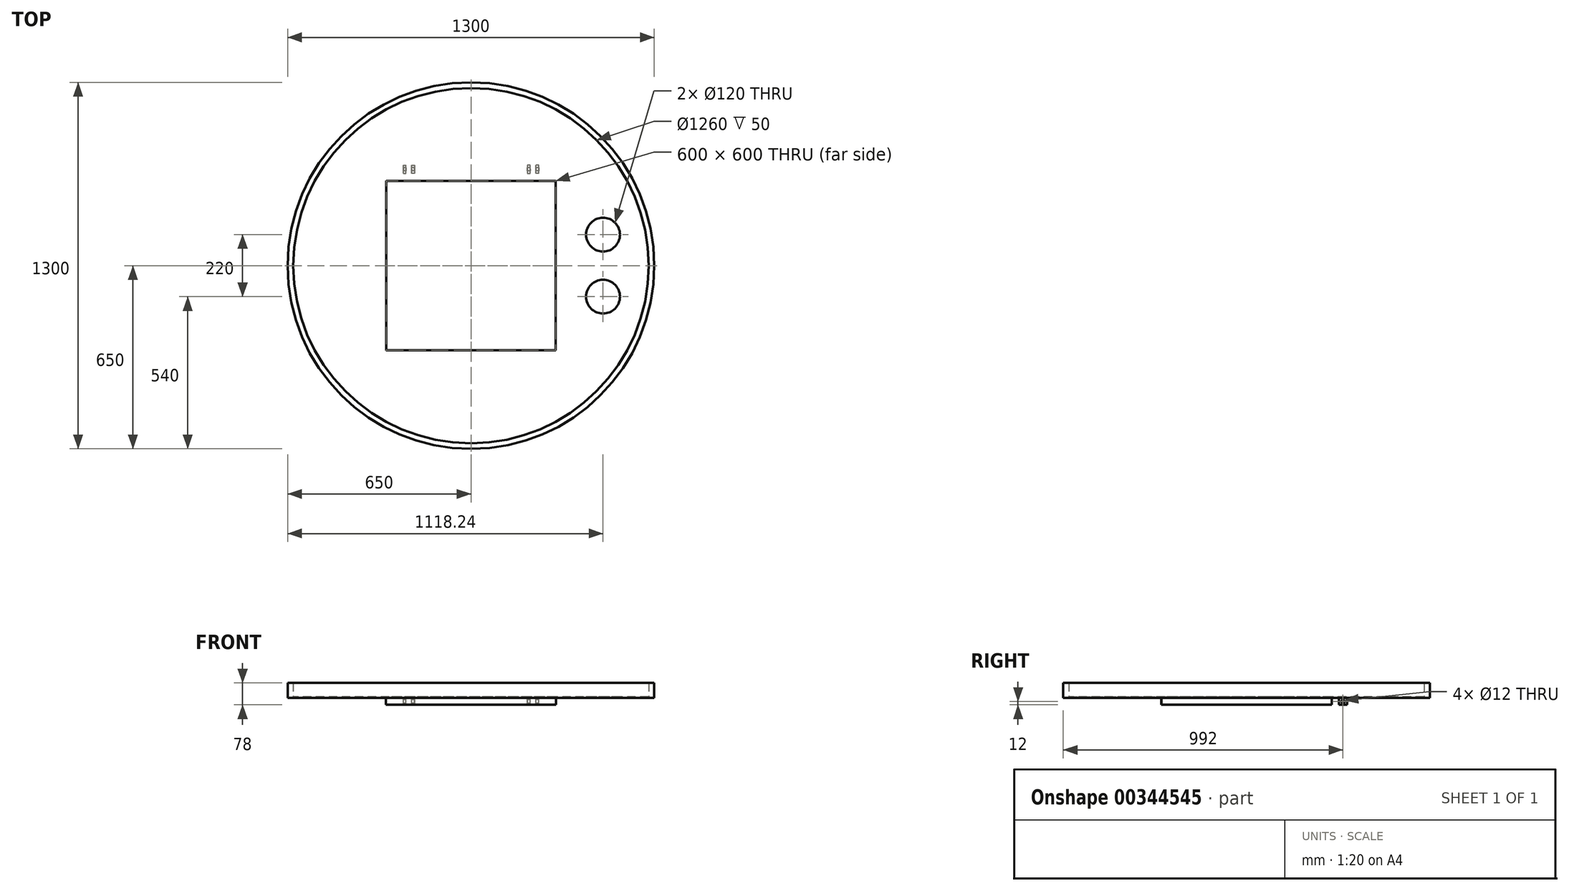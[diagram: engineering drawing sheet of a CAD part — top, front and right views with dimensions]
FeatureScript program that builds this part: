
annotation { "Feature Type Name" : "Feature", "Feature Type Description" : "" }
export const myFeature = defineFeature(function(context is Context, id is Id, definition is map)
    precondition{}
    {
        {
            var Q0;
            Q0=qCreatedBy(makeId("Top.planeOp"),FACE);
            var sketch = newSketch(context, id + "F0", { "sketchPlane" : qUnion([Q0])});
            skCircle(sketch, "E0", {"center": v(0, 0) * mm, "radius": 650 * mm});
            skSolve(sketch);
        }
        {
            var Q0;
            Q0=makeQuery(id+"F0.imprint","IMPRINT",FACE,{"disambiguationData":[TD([[makeQuery(id+"F0.imprint","IMPRINT",EDGE,{"derivedFrom":sQuery(id+"F0.wireOp",EDGE,"E0")}),1.0]])]});
            extrude(context, id + "F1", {"entities" : qUnion([Q0]), "depth" : 3 * mm});
        }
        {
            var Q0;
            Q0=makeQuery(id+"F1.opExtrude","CAP_FACE",FACE,{"disambiguationData":[OSD([sQuery(id+"F0.wireOp",EDGE,"E0")])],"isStart":false});
            var sketch = newSketch(context, id + "F2", { "sketchPlane" : qUnion([Q0])});
            skCircle(sketch, "E1", {"center": v(0, 0) * mm, "radius": 630 * mm});
            skCircle(sketch, "E2.0", {"center": v(0, 0) * mm, "radius": 650 * mm});
            skSolve(sketch);
        }
        {
            var Q0;
            Q0=makeQuery(id+"F2.imprint","IMPRINT",FACE,{"disambiguationData":[TD([[makeQuery(id+"F2.imprint","IMPRINT",EDGE,{"derivedFrom":sQuery(id+"F2.wireOp",EDGE,"E1")}),-1.0]])]});
            extrude(context, id + "F3", {"entities" : qUnion([Q0]), "operationType" : NewBodyOperationType.ADD, "depth" : 50 * mm});
        }
        {
            var Q0;
            Q0=makeQuery(id+"F1.opExtrude","CAP_FACE",FACE,{"disambiguationData":[OSD([sQuery(id+"F0.wireOp",EDGE,"E0")])],"isStart":true});
            var sketch = newSketch(context, id + "F4", { "sketchPlane" : qUnion([Q0])});
            skLineSegment(sketch, "E3.bottom", {"start": v(-300, 300) * mm, "end": v(300, 300) * mm});
            skLineSegment(sketch, "E3.top", {"start": v(-300, -300) * mm, "end": v(300, -300) * mm});
            skLineSegment(sketch, "E3.left", {"start": v(-300, 300) * mm, "end": v(-300, -300) * mm});
            skLineSegment(sketch, "E3.right", {"start": v(300, 300) * mm, "end": v(300, -300) * mm});
            skCircle(sketch, "E4", {"center": v(468.24, 110) * mm, "radius": 60 * mm});
            skCircle(sketch, "E5", {"center": v(468.24, -110) * mm, "radius": 60 * mm});
            skSolve(sketch);
        }
        {
            var Q0;
            Q0=makeQuery(id+"F4.imprint","IMPRINT",FACE,{"disambiguationData":[TD([[makeQuery(id+"F4.imprint","IMPRINT",EDGE,{"derivedFrom":sQuery(id+"F4.wireOp",EDGE,"E3.bottom")}),-1.0]])]});
            var Q1;
            Q1=makeQuery(id+"F4.imprint","IMPRINT",FACE,{"disambiguationData":[TD([[makeQuery(id+"F4.imprint","IMPRINT",EDGE,{"derivedFrom":sQuery(id+"F4.wireOp",EDGE,"E4")}),1.0]])]});
            var Q2;
            Q2=makeQuery(id+"F4.imprint","IMPRINT",FACE,{"disambiguationData":[TD([[makeQuery(id+"F4.imprint","IMPRINT",EDGE,{"derivedFrom":sQuery(id+"F4.wireOp",EDGE,"E5")}),1.0]])]});
            extrude(context, id + "F5", {"entities" : qUnion([Q0, Q1, Q2]), "operationType" : NewBodyOperationType.REMOVE, "oppositeDirection" : true, "depth" : 25 * mm});
        }
        {
            var Q0;
            Q0=makeQuery(id+"F1.opExtrude","CAP_FACE",FACE,{"disambiguationData":[OSD([sQuery(id+"F0.wireOp",EDGE,"E0")])],"isStart":true});
            var sketch = newSketch(context, id + "F6", { "sketchPlane" : qUnion([Q0])});
            skLineSegment(sketch, "E6.bottom", {"start": v(-302, 302) * mm, "end": v(302, 302) * mm});
            skLineSegment(sketch, "E6.top", {"start": v(-302, -302) * mm, "end": v(302, -302) * mm});
            skLineSegment(sketch, "E6.left", {"start": v(-302, 302) * mm, "end": v(-302, -302) * mm});
            skLineSegment(sketch, "E6.right", {"start": v(302, 302) * mm, "end": v(302, -302) * mm});
            skSolve(sketch);
        }
        {
            var Q0;
            Q0=makeQuery(id+"F6.imprint","IMPRINT",FACE,{"disambiguationData":[TD([[makeQuery(id+"F6.imprint","IMPRINT",EDGE,{"derivedFrom":sQuery(id+"F6.wireOp",EDGE,"E6.bottom")}),-1.0]])]});
            extrude(context, id + "F7", {"entities" : qUnion([Q0]), "operationType" : NewBodyOperationType.ADD, "depth" : 25 * mm});
        }
        {
            var Q0;
            Q0=makeQuery(id+"F1.opExtrude","CAP_FACE",FACE,{"disambiguationData":[OSD([sQuery(id+"F0.wireOp",EDGE,"E0")])],"isStart":true});
            var sketch = newSketch(context, id + "F8", { "sketchPlane" : qUnion([Q0])});
            skLineSegment(sketch, "E7.bottom", {"start": v(-240, -327) * mm, "end": v(-230, -327) * mm});
            skLineSegment(sketch, "E7.top", {"start": v(-240, -357) * mm, "end": v(-230, -357) * mm});
            skLineSegment(sketch, "E7.left", {"start": v(-240, -327) * mm, "end": v(-240, -357) * mm});
            skLineSegment(sketch, "E7.right", {"start": v(-230, -327) * mm, "end": v(-230, -357) * mm});
            skLineSegment(sketch, "E8", {"start": v(-210, -327) * mm, "end": v(-210, -357) * mm});
            skLineSegment(sketch, "E9", {"start": v(-210, -357) * mm, "end": v(-200, -357) * mm});
            skLineSegment(sketch, "E10", {"start": v(-200, -357) * mm, "end": v(-200, -327) * mm});
            skLineSegment(sketch, "E11", {"start": v(-200, -327) * mm, "end": v(-210, -327) * mm});
            skLineSegment(sketch, "E12.MirrorCS", {"start": v(230, -327) * mm, "end": v(230, -357) * mm});
            skLineSegment(sketch, "E13.MirrorCS", {"start": v(240, -327) * mm, "end": v(230, -327) * mm});
            skLineSegment(sketch, "E14.MirrorCS", {"start": v(240, -327) * mm, "end": v(240, -357) * mm});
            skLineSegment(sketch, "E15.MirrorCS", {"start": v(240, -357) * mm, "end": v(230, -357) * mm});
            skLineSegment(sketch, "E16.MirrorCS", {"start": v(210, -327) * mm, "end": v(210, -357) * mm});
            skLineSegment(sketch, "E17.MirrorCS", {"start": v(200, -327) * mm, "end": v(210, -327) * mm});
            skLineSegment(sketch, "E18.MirrorCS", {"start": v(200, -357) * mm, "end": v(200, -327) * mm});
            skLineSegment(sketch, "E19.MirrorCS", {"start": v(210, -357) * mm, "end": v(200, -357) * mm});
            skSolve(sketch);
        }
        {
            var Q0;
            Q0=makeQuery(id+"F8.imprint","IMPRINT",FACE,{"disambiguationData":[TD([[makeQuery(id+"F8.imprint","IMPRINT",EDGE,{"derivedFrom":sQuery(id+"F8.wireOp",EDGE,"E7.bottom")}),-1.0]])]});
            var Q1;
            Q1=makeQuery(id+"F8.imprint","IMPRINT",FACE,{"disambiguationData":[TD([[makeQuery(id+"F8.imprint","IMPRINT",EDGE,{"derivedFrom":sQuery(id+"F8.wireOp",EDGE,"E8")}),1.0]])]});
            var Q2;
            Q2=makeQuery(id+"F8.imprint","IMPRINT",FACE,{"disambiguationData":[TD([[makeQuery(id+"F8.imprint","IMPRINT",EDGE,{"derivedFrom":sQuery(id+"F8.wireOp",EDGE,"E16.MirrorCS")}),-1.0]])]});
            var Q3;
            Q3=makeQuery(id+"F8.imprint","IMPRINT",FACE,{"disambiguationData":[TD([[makeQuery(id+"F8.imprint","IMPRINT",EDGE,{"derivedFrom":sQuery(id+"F8.wireOp",EDGE,"E12.MirrorCS")}),1.0]])]});
            extrude(context, id + "F9", {"entities" : qUnion([Q0, Q1, Q2, Q3]), "operationType" : NewBodyOperationType.ADD, "depth" : 25 * mm});
        }
        {
            var Q0;
            Q0=qCreatedBy(makeId("Right.planeOp"),FACE);
            var sketch = newSketch(context, id + "F10", { "sketchPlane" : qUnion([Q0])});
            skPoint(sketch, "E20.0", {"position": v(342, -25) * mm});
            skLineSegment(sketch, "E21.0.0", {"start": v(357, 0) * mm, "end": v(327, 0) * mm});
            skLineSegment(sketch, "E21.0.1", {"start": v(327, 0) * mm, "end": v(327, -25) * mm});
            skLineSegment(sketch, "E21.0.2", {"start": v(327, -25) * mm, "end": v(357, -25) * mm});
            skLineSegment(sketch, "E21.0.3", {"start": v(357, -25) * mm, "end": v(357, 0) * mm});
            skCircle(sketch, "E22", {"center": v(342, -13) * mm, "radius": 6 * mm});
            skSolve(sketch);
        }
        {
            var Q0;
            Q0=makeQuery(id+"F10.imprint","IMPRINT",FACE,{"disambiguationData":[TD([[makeQuery(id+"F10.imprint","IMPRINT",EDGE,{"derivedFrom":sQuery(id+"F10.wireOp",EDGE,"E22")}),1.0]])]});
            extrude(context, id + "F11", {"entities" : qUnion([Q0]), "operationType" : NewBodyOperationType.REMOVE, "endBound" : BoundingType.SYMMETRIC, "depth" : 1000 * mm});
        }
    });
